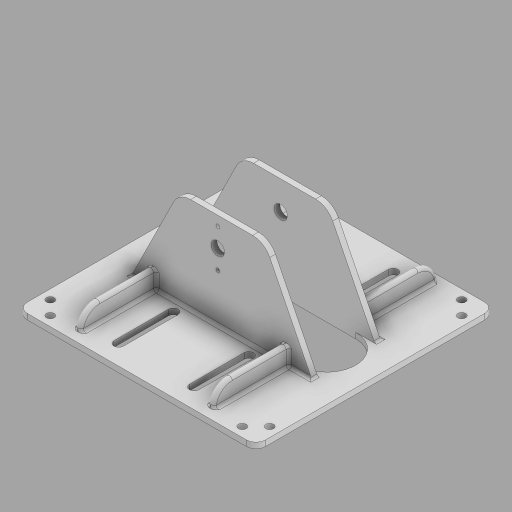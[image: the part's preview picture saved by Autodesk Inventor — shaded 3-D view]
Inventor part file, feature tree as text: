
AUTODESK INVENTOR PART (.ipt)
format: ipt  version: 2023.2 (Build 272271030, 271C)  size: 1,079,808 bytes
history: native  units: mm
features: extrude x9, projected_geometry x6, fillet x5, sketch x3
ambient origin geometry x8: Origin, YZ Plane, XZ Plane, XY Plane, X Axis, Y Axis, Z Axis, Center Point
bodies: Solid1 (feature_tree)
feature tree (23):
  extrude  "Extrusion1"  Depth=120.0mm
  sketch  "Sketch3"  dims[d0=120.0mm d1=120.0mm]
  extrude  "Extrusion2"  Depth=3.0mm
  extrude  "Extrusion4"  Depth=1.5mm
  extrude  "Extrusion5"  Depth=10.0mm TaperAngle=0.0deg
  extrude  "Extrusion6"  Depth=1.5mm TaperAngle=0.0deg
  fillet  "Fillet1"  Radius=50.0mm
  extrude  "Extrusion8"  Depth=10.0mm TaperAngle=0.0deg
  fillet  "Fillet3"  Radius=10.0mm
  fillet  "Fillet4"  Radius=4.1mm
  extrude  "Extrusion12"  Depth=1.5mm
  extrude  "Extrusion13"  Depth=1.5mm TaperAngle=0.0deg
  fillet  "Fillet7"  Radius=5.0mm
  fillet  "Fillet8"  Radius=3.0mm
  extrude  "Extrusion14"  Depth=3.0mm
  projected_geometry  "Projected Loop1"
  projected_geometry  "Projected Loop3"
  projected_geometry  "Projected Loop5"
  projected_geometry  "Projected Loop9"
  sketch  "Sketch22"  dims[d4=3.0mm d5=0.0mm d6=3.0mm]
  projected_geometry  "Projected Loop10"
  sketch  "Sketch25"  dims[d12=5.0mm d14=3.5mm d15=10.0mm d16=0.0mm d20=50.0mm d21=0.0mm d22=50.0mm d23=0.0mm d24=10.0mm d25=0.0mm d26=10.0mm d31=4.1mm d33=4.1mm d35=100.0mm d36=0.0mm d37=5.0mm d41=3.0mm d43=3.0mm d45=3.0mm d46=10.0mm d54=7.0mm d55=100.0mm d56=0.0mm d59=30.0mm d62=125.0mm d63=125.0mm d64=3.0mm d65=0.0mm d66=5.0mm d67=4.1mm d68=4.1mm d69=4.1mm d70=4.1mm d71=4.1mm d72=4.1mm d75=3.0mm d76=3.0mm d77=1.5mm d78=9.97mm d79=2.0mm d80=9.97mm d81=2.0mm d82=2.0mm d83=0.0mm]
  projected_geometry  "Projected Loop13"
